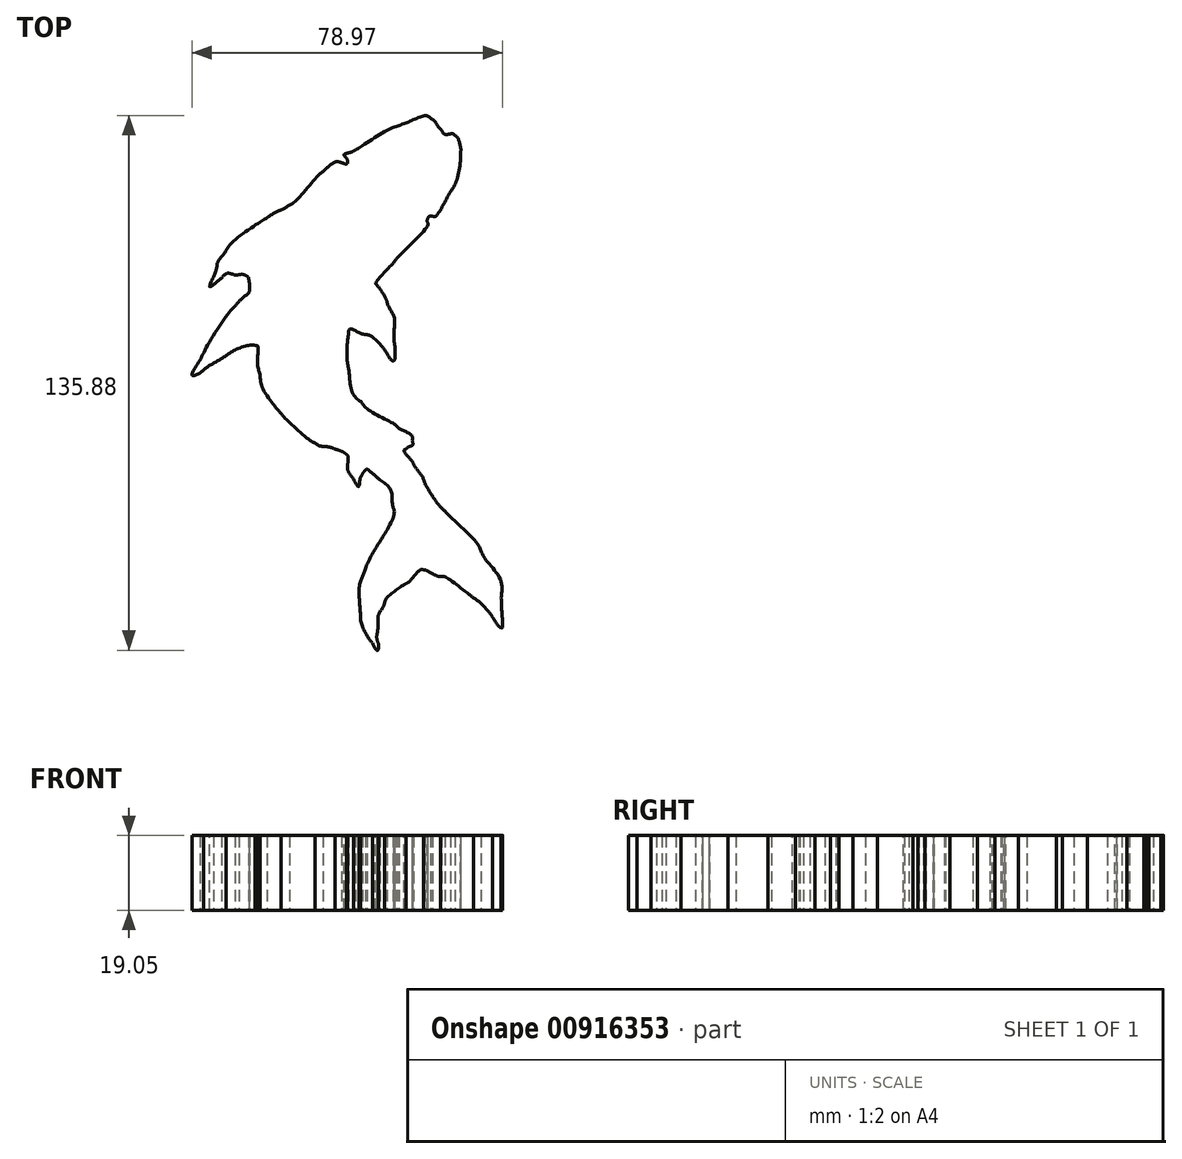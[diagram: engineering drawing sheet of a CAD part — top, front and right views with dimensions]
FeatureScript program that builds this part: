
annotation { "Feature Type Name" : "Feature", "Feature Type Description" : "" }
export const myFeature = defineFeature(function(context is Context, id is Id, definition is map)
    precondition{}
    {
        {
            var Q0;
            Q0=qCreatedBy(makeId("Top.planeOp"),FACE);
            var sketch = newSketch(context, id + "F0", { "sketchPlane" : qUnion([Q0])});
            skFitSpline(sketch, "E0", {"points": [v(18.02, -25.62) * mm, v(19.99, -28.85) * mm, v(21.7, -31.2) * mm, v(23.14, -32.64) * mm]});
            skFitSpline(sketch, "E1", {"points": [v(23.14, -32.64) * mm, v(25.3, -34.8) * mm, v(31.02, -40.43) * mm, v(32.32, -42.77) * mm]});
            skFitSpline(sketch, "E2", {"points": [v(32.32, -42.77) * mm, v(33.62, -45.11) * mm, v(37.17, -49.88) * mm, v(37.44, -54.73) * mm]});
            skFitSpline(sketch, "E3", {"points": [v(37.44, -54.73) * mm, v(37.7, -59.58) * mm, v(37.7, -62.27) * mm, v(37.35, -62.18) * mm]});
            skFitSpline(sketch, "E4", {"points": [v(37.35, -62.18) * mm, v(37, -62.1) * mm, v(35.7, -60.28) * mm, v(35.18, -59.5) * mm]});
            skFitSpline(sketch, "E5", {"points": [v(35.18, -59.5) * mm, v(34.66, -58.72) * mm, v(32.24, -56.03) * mm, v(30.42, -54.64) * mm]});
            skFitSpline(sketch, "E6", {"points": [v(30.42, -54.64) * mm, v(28.6, -53.26) * mm, v(23.14, -49.36) * mm, v(22.01, -49.19) * mm]});
            skFitSpline(sketch, "E7", {"points": [v(22.01, -49.19) * mm, v(20.89, -49.01) * mm, v(18.37, -47.63) * mm, v(17.68, -47.54) * mm]});
            skFitSpline(sketch, "E8", {"points": [v(17.68, -47.54) * mm, v(16.99, -47.45) * mm, v(14.13, -50.48) * mm, v(13.26, -51) * mm]});
            skFitSpline(sketch, "E9", {"points": [v(13.26, -51) * mm, v(12.4, -51.53) * mm, v(8.32, -54.73) * mm, v(7.8, -55.94) * mm]});
            skFitSpline(sketch, "E10", {"points": [v(7.8, -55.94) * mm, v(7.28, -57.16) * mm, v(6.24, -59.06) * mm, v(6.16, -60.97) * mm]});
            skFitSpline(sketch, "E11", {"points": [v(6.16, -60.97) * mm, v(6.07, -62.88) * mm, v(5.8, -64.7) * mm, v(6.07, -65.82) * mm]});
            skFitSpline(sketch, "E12", {"points": [v(6.07, -65.82) * mm, v(6.33, -66.95) * mm, v(5.98, -67.99) * mm, v(4.68, -66.17) * mm]});
            skFitSpline(sketch, "E13", {"points": [v(4.68, -66.17) * mm, v(3.38, -64.35) * mm, v(1.82, -60.7) * mm, v(1.65, -58.46) * mm]});
            skFitSpline(sketch, "E14", {"points": [v(1.65, -58.46) * mm, v(1.48, -56.2) * mm, v(1.39, -51.7) * mm, v(2.26, -49.18) * mm]});
            skFitSpline(sketch, "E15", {"points": [v(2.26, -49.18) * mm, v(3.12, -46.67) * mm, v(5.29, -42.43) * mm, v(6.33, -40.78) * mm]});
            skFitSpline(sketch, "E16", {"points": [v(6.33, -40.78) * mm, v(7.37, -39.13) * mm, v(10.23, -33.42) * mm, v(9.97, -31.68) * mm]});
            skFitSpline(sketch, "E17", {"points": [v(9.97, -31.68) * mm, v(9.7, -29.95) * mm, v(9.36, -27.18) * mm, v(6.68, -24.75) * mm]});
            skFitSpline(sketch, "E18", {"points": [v(6.68, -24.75) * mm, v(4.89, -23.13) * mm, v(3.76, -22.18) * mm, v(3.3, -21.9) * mm]});
            skFitSpline(sketch, "E19", {"points": [v(3.3, -21.9) * mm, v(2.72, -22.41) * mm, v(2.29, -22.96) * mm, v(2, -23.54) * mm]});
            skFitSpline(sketch, "E20", {"points": [v(2, -23.54) * mm, v(1.56, -24.4) * mm, v(1.22, -26.4) * mm, v(-0.08, -24.5) * mm]});
            skFitSpline(sketch, "E21", {"points": [v(-0.08, -24.5) * mm, v(-1.38, -22.58) * mm, v(-1.64, -21.72) * mm, v(-1.56, -20.6) * mm]});
            skFitSpline(sketch, "E22", {"points": [v(-1.56, -20.6) * mm, v(-1.47, -19.47) * mm, v(-1.64, -18.34) * mm, v(-1.9, -18.17) * mm]});
            skFitSpline(sketch, "E23", {"points": [v(-1.9, -18.17) * mm, v(-2.16, -18) * mm, v(-2.94, -17.47) * mm, v(-4.76, -16.87) * mm]});
            skFitSpline(sketch, "E24", {"points": [v(-4.76, -16.87) * mm, v(-6.58, -16.26) * mm, v(-8.49, -16.09) * mm, v(-9.87, -15.3) * mm]});
            skFitSpline(sketch, "E25", {"points": [v(-9.87, -15.3) * mm, v(-11.26, -14.53) * mm, v(-17.15, -9.33) * mm, v(-18.45, -7.86) * mm]});
            skFitSpline(sketch, "E26", {"points": [v(-18.45, -7.86) * mm, v(-19.75, -6.38) * mm, v(-23.13, -1.44) * mm, v(-23.82, 2.1) * mm]});
            skFitSpline(sketch, "E27", {"points": [v(-23.82, 2.1) * mm, v(-24.52, 5.66) * mm, v(-24.43, 9.3) * mm, v(-25.12, 9.47) * mm]});
            skFitSpline(sketch, "E28", {"points": [v(-25.12, 9.47) * mm, v(-25.82, 9.65) * mm, v(-29.98, 8.43) * mm, v(-32.49, 6.87) * mm]});
            skFitSpline(sketch, "E29", {"points": [v(-32.49, 6.87) * mm, v(-35, 5.31) * mm, v(-37.25, 4.01) * mm, v(-38.2, 3.23) * mm]});
            skFitSpline(sketch, "E30", {"points": [v(-38.2, 3.23) * mm, v(-39.16, 2.45) * mm, v(-41.07, 1.85) * mm, v(-39.07, 5.75) * mm]});
            skFitSpline(sketch, "E31", {"points": [v(-39.07, 5.75) * mm, v(-37.08, 9.65) * mm, v(-31.88, 17.62) * mm, v(-30.15, 19.52) * mm]});
            skFitSpline(sketch, "E32", {"points": [v(-30.15, 19.52) * mm, v(-28.42, 21.43) * mm, v(-26.6, 23) * mm, v(-26.5, 23.77) * mm]});
            skFitSpline(sketch, "E33", {"points": [v(-26.5, 23.77) * mm, v(-26.45, 24.3) * mm, v(-26.54, 25.3) * mm, v(-26.77, 26.8) * mm]});
            skFitSpline(sketch, "E34", {"points": [v(-26.77, 26.8) * mm, v(-27.52, 27.32) * mm, v(-28.3, 27.56) * mm, v(-29.1, 27.5) * mm]});
            skFitSpline(sketch, "E35", {"points": [v(-29.1, 27.5) * mm, v(-30.32, 27.41) * mm, v(-32.14, 27.84) * mm, v(-33.62, 26.63) * mm]});
            skFitSpline(sketch, "E36", {"points": [v(-33.62, 26.63) * mm, v(-35.09, 25.42) * mm, v(-36.56, 24.38) * mm, v(-35.7, 26.9) * mm]});
            skFitSpline(sketch, "E37", {"points": [v(-35.7, 26.9) * mm, v(-34.83, 29.4) * mm, v(-34.65, 30.53) * mm, v(-32.75, 33.13) * mm]});
            skFitSpline(sketch, "E38", {"points": [v(-32.75, 33.13) * mm, v(-30.84, 35.73) * mm, v(-24.52, 40.4) * mm, v(-22, 41.97) * mm]});
            skFitSpline(sketch, "E39", {"points": [v(-22, 41.97) * mm, v(-19.5, 43.53) * mm, v(-18.1, 44.05) * mm, v(-16.37, 45.17) * mm]});
            skFitSpline(sketch, "E40", {"points": [v(-16.37, 45.17) * mm, v(-14.64, 46.3) * mm, v(-9.44, 52.28) * mm, v(-7.88, 53.67) * mm]});
            skFitSpline(sketch, "E41", {"points": [v(-7.88, 53.67) * mm, v(-6.32, 55.05) * mm, v(-4.5, 56.18) * mm, v(-3.11, 55.92) * mm]});
            skFitSpline(sketch, "E42", {"points": [v(-3.11, 55.92) * mm, v(-1.73, 55.66) * mm, v(-1.64, 56.61) * mm, v(-2.07, 57.3) * mm]});
            skFitSpline(sketch, "E43", {"points": [v(-2.07, 57.3) * mm, v(-2.5, 58) * mm, v(-0.69, 58.6) * mm, v(0.44, 59.21) * mm]});
            skFitSpline(sketch, "E44", {"points": [v(0.44, 59.21) * mm, v(1.56, 59.82) * mm, v(7.89, 63.9) * mm, v(11.53, 65.36) * mm]});
            skFitSpline(sketch, "E45", {"points": [v(11.53, 65.36) * mm, v(15.17, 66.84) * mm, v(18.46, 67.88) * mm, v(19.5, 67.18) * mm]});
            skFitSpline(sketch, "E46", {"points": [v(19.5, 67.18) * mm, v(20.54, 66.49) * mm, v(21.32, 65.19) * mm, v(22.27, 64.15) * mm]});
            skFitSpline(sketch, "E47", {"points": [v(22.27, 64.15) * mm, v(23.23, 63.1) * mm, v(25.05, 63.28) * mm, v(25.65, 62.85) * mm]});
            skFitSpline(sketch, "E48", {"points": [v(25.65, 62.85) * mm, v(26.26, 62.42) * mm, v(27.13, 59.73) * mm, v(27.13, 58.6) * mm]});
            skFitSpline(sketch, "E49", {"points": [v(27.13, 58.6) * mm, v(27.13, 57.48) * mm, v(26.17, 51.59) * mm, v(24.53, 48.55) * mm]});
            skFitSpline(sketch, "E50", {"points": [v(24.53, 48.55) * mm, v(22.88, 45.52) * mm, v(20.71, 42.31) * mm, v(19.93, 42.31) * mm]});
            skFitSpline(sketch, "E51", {"points": [v(19.93, 42.31) * mm, v(19.15, 42.31) * mm, v(18.63, 41.36) * mm, v(18.72, 40.67) * mm]});
            skFitSpline(sketch, "E52", {"points": [v(18.72, 40.67) * mm, v(18.8, 39.98) * mm, v(11.53, 32.26) * mm, v(10.49, 31.05) * mm]});
            skFitSpline(sketch, "E53", {"points": [v(10.49, 31.05) * mm, v(9.45, 29.84) * mm, v(5.55, 25.33) * mm, v(5.72, 25.07) * mm]});
            skFitSpline(sketch, "E54", {"points": [v(5.72, 25.07) * mm, v(5.9, 24.81) * mm, v(7.9, 21.95) * mm, v(8.41, 20.57) * mm]});
            skFitSpline(sketch, "E55", {"points": [v(8.41, 20.57) * mm, v(8.93, 19.18) * mm, v(10.23, 16.67) * mm, v(10.23, 13.63) * mm]});
            skFitSpline(sketch, "E56", {"points": [v(10.23, 13.63) * mm, v(10.23, 10.6) * mm, v(10.49, 8.7) * mm, v(10.4, 7.22) * mm]});
            skFitSpline(sketch, "E57", {"points": [v(10.4, 7.22) * mm, v(10.32, 5.75) * mm, v(9.8, 5.58) * mm, v(8.41, 7.48) * mm]});
            skFitSpline(sketch, "E58", {"points": [v(8.41, 7.48) * mm, v(7.02, 9.39) * mm, v(4.25, 11.9) * mm, v(2.95, 12.25) * mm]});
            skFitSpline(sketch, "E59", {"points": [v(2.95, 12.25) * mm, v(1.65, 12.6) * mm, v(-1.03, 13.63) * mm, v(-1.3, 12.42) * mm]});
            skFitSpline(sketch, "E60", {"points": [v(-1.3, 12.42) * mm, v(-1.55, 11.2) * mm, v(-1.73, 6) * mm, v(-1.47, 4.27) * mm]});
            skFitSpline(sketch, "E61", {"points": [v(-1.47, 4.27) * mm, v(-1.2, 2.54) * mm, v(-0.34, -2.57) * mm, v(1.83, -4.82) * mm]});
            skFitSpline(sketch, "E62", {"points": [v(1.83, -4.82) * mm, v(4, -7.08) * mm, v(10.23, -10.46) * mm, v(10.92, -11.06) * mm]});
            skFitSpline(sketch, "E63", {"points": [v(10.92, -11.06) * mm, v(11.62, -11.67) * mm, v(14.73, -13.4) * mm, v(14.82, -14.62) * mm]});
            skFitSpline(sketch, "E64", {"points": [v(14.82, -14.62) * mm, v(14.9, -15.83) * mm, v(13.96, -16.26) * mm, v(13.35, -16.78) * mm]});
            skFitSpline(sketch, "E65", {"points": [v(13.35, -16.78) * mm, v(12.74, -17.3) * mm, v(14.4, -19.47) * mm, v(15.17, -20.68) * mm]});
            skFitSpline(sketch, "E66", {"points": [v(15.17, -20.68) * mm, v(15.95, -21.9) * mm, v(17.5, -24.05) * mm, v(18.02, -25.62) * mm]});
            skSolve(sketch);
        }
        {
            var Q0;
            Q0=makeQuery(id+"F0.imprint","IMPRINT",FACE,{"disambiguationData":[TD([[makeQuery(id+"F0.imprint","IMPRINT",EDGE,{"derivedFrom":sQuery(id+"F0.wireOp",EDGE,"E0")}),-1.0]])]});
            extrude(context, id + "F1", {"entities" : qUnion([Q0]), "depth" : 19.05 * mm, "offsetDistance" : 25.4 * mm});
        }
    });
